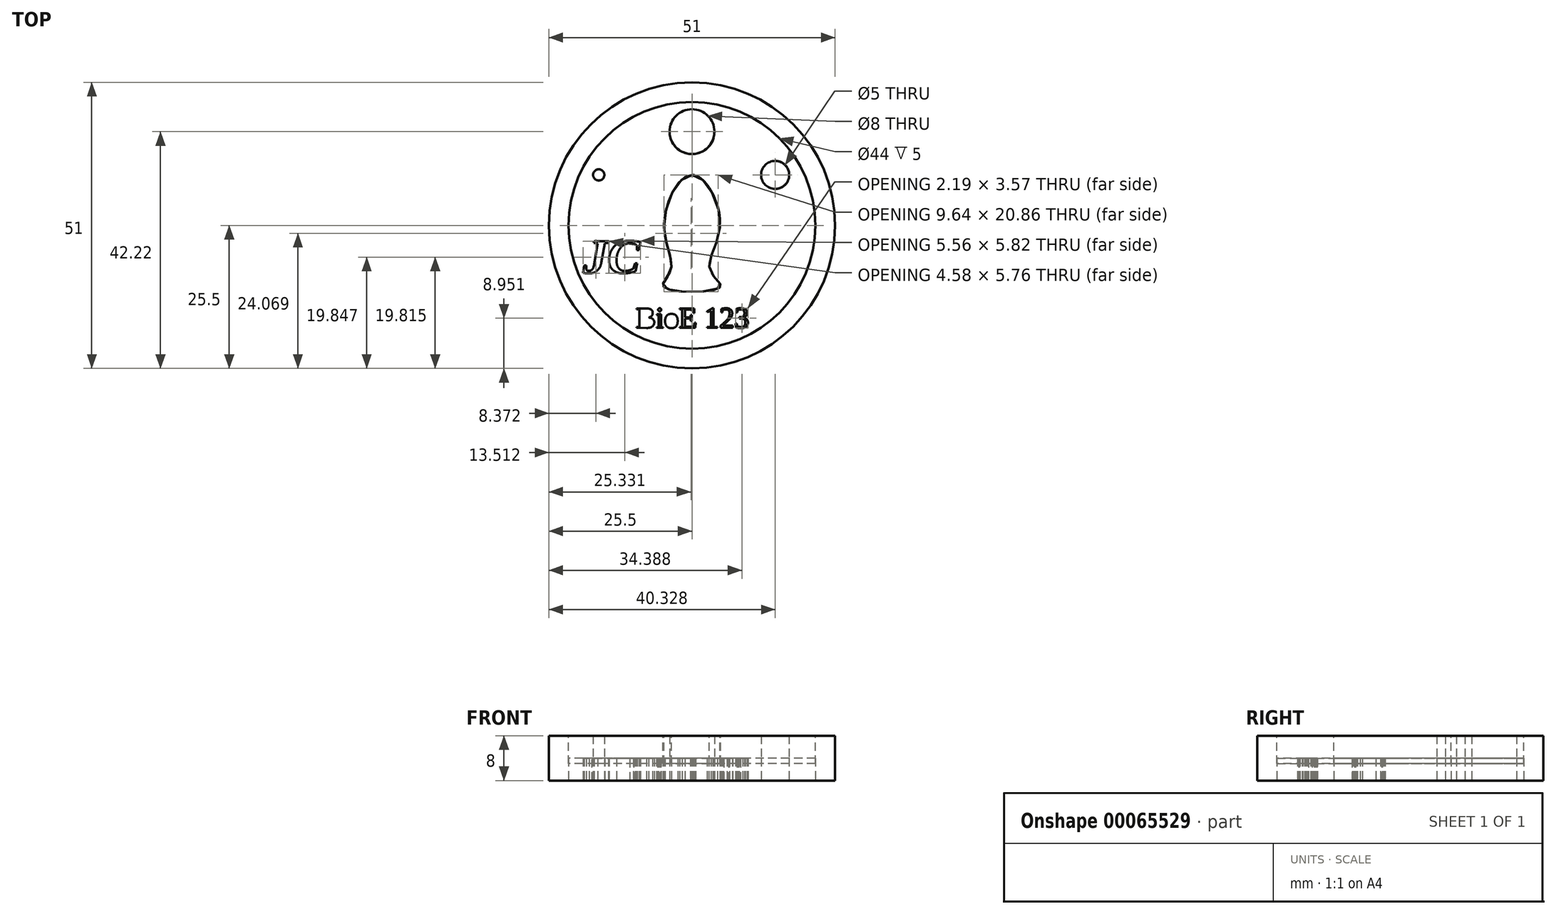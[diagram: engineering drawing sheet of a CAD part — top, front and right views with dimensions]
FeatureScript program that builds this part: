
annotation { "Feature Type Name" : "Feature", "Feature Type Description" : "" }
export const myFeature = defineFeature(function(context is Context, id is Id, definition is map)
    precondition{}
    {
        {
            var Q0;
            Q0=qCreatedBy(makeId("Top.planeOp"),FACE);
            var sketch = newSketch(context, id + "F0", { "sketchPlane" : qUnion([Q0])});
            skCircle(sketch, "E0", {"center": v(0, 0) * mm, "radius": 25.5 * mm});
            skSolve(sketch);
        }
        {
            var Q0;
            Q0=makeQuery(id+"F0.imprint","IMPRINT",FACE,{"disambiguationData":[TD([[makeQuery(id+"F0.imprint","IMPRINT",EDGE,{"derivedFrom":sQuery(id+"F0.wireOp",EDGE,"E0")}),1.0]])]});
            extrude(context, id + "F1", {"entities" : qUnion([Q0]), "depth" : 8 * mm});
        }
        {
            var Q0;
            Q0=makeQuery(id+"F1.opExtrude","CAP_FACE",FACE,{"disambiguationData":[OSD([sQuery(id+"F0.wireOp",EDGE,"E0")])],"isStart":false});
            var sketch = newSketch(context, id + "F2", { "sketchPlane" : qUnion([Q0])});
            skCircle(sketch, "E1", {"center": v(0, 0) * mm, "radius": 22 * mm});
            skSolve(sketch);
        }
        {
            var Q0;
            Q0 = qSketchRegion(id + "F2", true);
            extrude(context, id + "F3", {"entities" : qUnion([Q0]), "operationType" : NewBodyOperationType.REMOVE, "oppositeDirection" : true, "depth" : 5 * mm});
        }
        {
            var Q0;
            Q0=makeQuery(id+"F3.boolean.opBoolean","COPY",FACE,{"derivedFrom":makeQuery(id+"F3.opExtrude","CAP_FACE",FACE,{"disambiguationData":[OSD([sQuery(id+"F2.wireOp",EDGE,"E1")])],"isStart":false})});
            var sketch = newSketch(context, id + "F4", { "sketchPlane" : qUnion([Q0])});
            skFitSpline(sketch, "E2", {"points": [v(0, 9) * mm, v(-5, 0) * mm, v(-3.8, -8) * mm, v(-5, -11) * mm, v(5, -11) * mm, v(3.2, -8) * mm, v(5, 0) * mm, v(0, 9) * mm]});
            skCircle(sketch, "E3", {"center": v(-16.62, 9) * mm, "radius": 1 * mm});
            skCircle(sketch, "E4", {"center": v(0, 16.72) * mm, "radius": 4 * mm});
            skCircle(sketch, "E5", {"center": v(14.83, 9) * mm, "radius": 2.5 * mm});
            skSolve(sketch);
        }
        {
            var Q0;
            Q0 = qSketchRegion(id + "F4", true);
            var Q1;
            Q1=makeQuery(id+"F1.opExtrude","CAP_FACE",FACE,{"disambiguationData":[OSD([sQuery(id+"F0.wireOp",EDGE,"E0")])],"isStart":false});
            extrude(context, id + "F5", {"entities" : qUnion([Q0]), "operationType" : NewBodyOperationType.ADD, "endBound" : BoundingType.UP_TO_SURFACE, "endBoundEntityFace" : qUnion([Q1]), "depth" : 5 * mm});
        }
        {
            var Q0;
            Q0=qCreatedBy(makeId("Top.planeOp"),FACE);
            var sketch = newSketch(context, id + "F6", { "sketchPlane" : qUnion([Q0])});
            skCircle(sketch, "E6", {"center": v(-16.62, 9) * mm, "radius": 1 * mm});
            skCircle(sketch, "E7", {"center": v(14.83, 9) * mm, "radius": 2.5 * mm});
            skCircle(sketch, "E8", {"center": v(0, 16.72) * mm, "radius": 4 * mm});
            skFitSpline(sketch, "E9", {"points": [v(0, 9) * mm, v(-5, 0) * mm, v(-3.8, -8) * mm, v(-5, -11) * mm, v(5.01, -11) * mm, v(3.2, -8) * mm, v(5, 0) * mm, v(0, 9) * mm]});
            skText(sketch, "E10", { "text": "JC", "fontName": "Tinos-BoldItalic.ttf"});
            skText(sketch, "E11", { "text": "BioE 123", "fontName": "Tinos-Regular.ttf"});
            skCircle(sketch, "E12", {"center": v(0, 0) * mm, "radius": 22 * mm});
            const initialGuessF6  = {"E10": [-0.0194, -0.00848, 1, 0, 0.00624], "E11": [-0.01, -0.01828, 1, 0, 0.00382]};
            skSetInitialGuess(sketch, initialGuessF6);
            skSolve(sketch);
        }
        {
            var Q0;
            Q0=makeQuery(id+"F6.imprint","IMPRINT",FACE,{"disambiguationData":[TD([[makeQuery(id+"F6.imprint","IMPRINT",EDGE,{"derivedFrom":sQuery(id+"F6.wireOp",EDGE,"E6")}),-1.0]])]});
            extrude(context, id + "F7", {"entities" : qUnion([Q0]), "depth" : 4 * mm});
        }
    });
